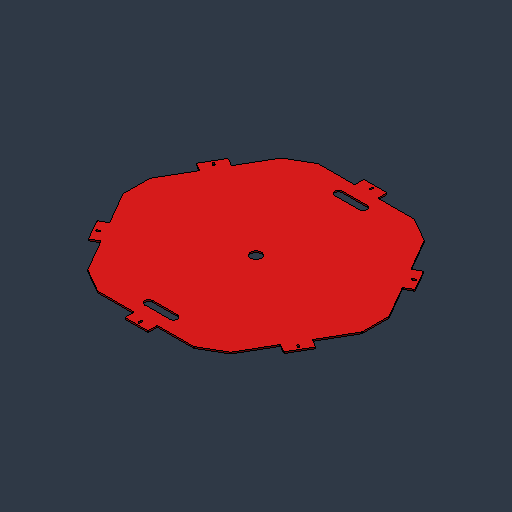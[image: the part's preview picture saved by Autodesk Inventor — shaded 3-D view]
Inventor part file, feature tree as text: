
AUTODESK INVENTOR PART (.ipt)
format: ipt  version: 2024.3 (Build 283343000, 343)  size: 160,256 bytes
history: native  units: mm (DEFAULTED — no unit token found)
features: fillet x1
ambient origin geometry x8: Origin, YZ Plane, XZ Plane, XY Plane, X Axis, Y Axis, Z Axis, Center Point
bodies: Solid1 (feature_tree)
feature tree (1):
  fillet  "Fillet2"  [1 undecoded]
note: 1 required parameter value undecoded (feature->parameter linkage not recoverable at this tier; creation-order binding heuristic only, values carry confidence <= 0.55)
